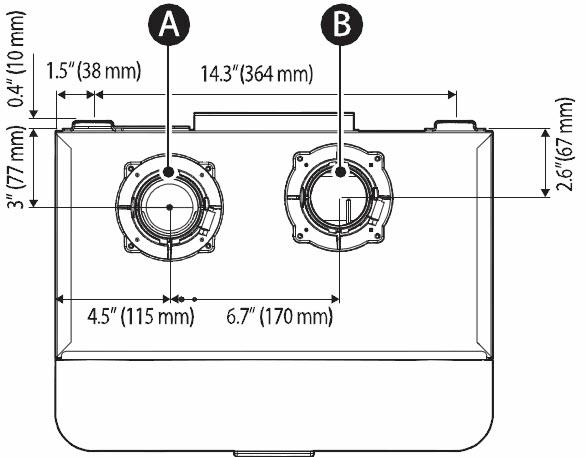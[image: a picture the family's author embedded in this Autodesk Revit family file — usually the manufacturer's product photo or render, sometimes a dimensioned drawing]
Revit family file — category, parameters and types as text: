
# Revit family: Water_Heater-Racks-Navien-NPE-5_Unit_Front---
name_source: partatom
category: Mechanical Equipment
revit_build: Autodesk Revit 2016 (Build: 20150220_1215(x64)
units: mm (PartAtom-declared; Revit-internal decimal feet)

## family parameters
Cut with Voids When Loaded = No
Host = Face
OmniClass Number = 23.65.35.11
OmniClass Title = Supply Water Heaters
Part Type = Normal
Room Calculation Point = No
Round Connector Dimension = Use Diameter
Shared = No

## types (4) — shared parameters
2" Exhaust/Intake = Yes
3" Exhaust/Intake = No
Apparent Load = 0 VA
Assembly Code = D3010500
Certifications = Energy Star | AHRI | CSA | CSA | NFS
Cold Water Inlet = 1"
Configuration = NPE_F5_3F2F
Default Elevation = 48 "
Depth = 23.8 "
Description = 5 Unit Front
Exhaust = 2"
Finish = Metal - Navien - White
Flow Rate = 1 GPM
Flow Rate Note = 35°F (19°C) temp rise: 11.2 GPM (42 L/m) | 45°F (25°C) temp rise: 8.7 GPM (33 L/m) | 67°F (36°C) temp rise: NPE-240A: 5.6 GPM(21 L/m), NPE-240S: 5.7 GPM(22 L/m)
Frequency = 60 Hz
Gas Inlet = 1"
Heating Capacity = 120000.0 Btu/h
Heating Capacity Note = 19,900–199,900 (BTU/H)
Height = 65.5 "
Hot Water Outlet = 1"
Ignition = Electronic ignition
Installation Type = Indoor
Intake = 2"
Keynote = 22 33 00.A1
Manifold(s) = (1) 30019040A + (1) 30019041A
Manufacturer = Navien, Inc.
Manufacturer Fax Number = (949) 420-0430
Natural Gas Manifold Pressure = -0.05" WC to -0.58" WC
Natural Gas Supply Pressure = 3.5"–10.5" WC
Number of Poles = 1
Phase = 1
Power Factor = 1
Product Documentation Link = https://www.navieninc.com
Product Name = NPE Series Tankless Water Heaters w/ Racks
Product Page URL = https://www.navieninc.com
Propane Gas Manifold Pressure = -0.10" WC to -0.78" WC
Propane Gas Supply Pressure = 8"–13" WC
Rack(s) = (1) GFFM-KDIZUS-003 + (4) GFFM-KDIZUS-004
Required Cascade Operation Accessory = (5) 30014367A (Common Vent Damper & Cascade Communication Cable) or (4) GXXX000546 (Individual Vent Cascade Communication Cable)
Type Comments = For Wall Mount RL Manifold systems- Exclude Base & Add-on Racks
URL = https://www.navieninc.com
Venting = Exhaust: 2" PVC, CPVC, PP, SS / 2" special gas vent type BH (Class II, A/B/C) | Intake: 2" PVC, CPVC, PP, SS / 2" special gas vent type BH (Class II, A/B/C) | Vent clearances: 0" to combustibles
Venting Type = Forced draft direct vent
Version = 2016 - v1.0.a
Voltage = 120 V
Water Pressure = 15–150 PSI
Wi-Fi Ready = NaviLink Wi-Fi Control: PBCM-AS-001
Width = 102.3 "

## per-type parameters (varying)
| type | Constraints | Model | Natural Gas | Propane Gas | Recirculation Inlet | Recirculation Inlet Visibility | Tankless Water Heaters | Weight |
| Natural Gas - Recirculating System - NPE-240A(Advanced)-NG | 6 | (5) NPE-240A-NG | Yes | No | 0" | Yes | (5) NPE-240A-NG | 82.00 lbf |
| Natural Gas - NPE-240S(Standard)-NG | 7 | (5) NPE-240S-NG | Yes | No | 1" | No | (5) NPE-240S-NG | 75.00 lbf |
| Propane Gas - Recirculating System - NPE-240A(Advanced)-LPG | 6 | (5) NPE-240A-LPG | No | Yes | 0" | Yes | (5) NPE-240A-LPG | 82.00 lbf |
| Propane Gas - NPE-240S(Standard)-LPG | 7 | (5) NPE-240S-LPG | No | Yes | 1" | No | (5) NPE-240S-LPG | 75.00 lbf |

## geometry (parser evidence)
native form markers: Sweep x20
no freeform markers — native parametric forms only
